# Revit family: PRO2XY - 5 BAR - Ox3 à 16
name_source: partatom
category: Equipement de génie climatique
units: mm (PartAtom-declared; Revit-internal decimal feet)

## family parameters
Basée sur le plan de construction = Non
Classification = Aucun
Cote de connecteur circulaire = Utiliser le diamètre
Couper avec des vides une fois chargée = Non
Partagée = Non
Repere pour localisation dans la piece = Non
Toujours verticalement = Oui
Type d'élément = Normal

## types (4) — shared parameters
Fabricant = Mil's
zero-valued in all types: Elévation par défaut

## per-type parameters (varying)
| type | Distance Ballon tapon | Modèle | Type Ballon Réservoir | Type ballon mélange GAZ | Type de support | distance Armoire Elec |
| OX3 | 330 mm | OX3 | Ballon : 200L | Ballon 70L mélange Gaz | Chassis générateur 3-4,5-7 M3 | 169 mm |
| OX5 | 355 mm  [stored 1.1647 ft] | OX3 | Ballon : 200L | Ballon 110L mélange Gaz | Chassis générateur 3-4,5-7 M3 | 194 mm |
| OX7 - OX9 | 469 mm | OX3 | Ballon : 500L | Ballon 160L mélange Gaz | Chassis générateur 3-4,5-7 M3 | 219 mm |
| OX13 - OX16 | 519 mm | OX13 - OX16 | Ballon : 500L | Ballon 295L mélange Gaz | Chassis générateur OX13 | 269 mm |

note: [stored X ft] marks values corroborated as IEEE doubles in the binary element streams (Revit-internal decimal feet)
